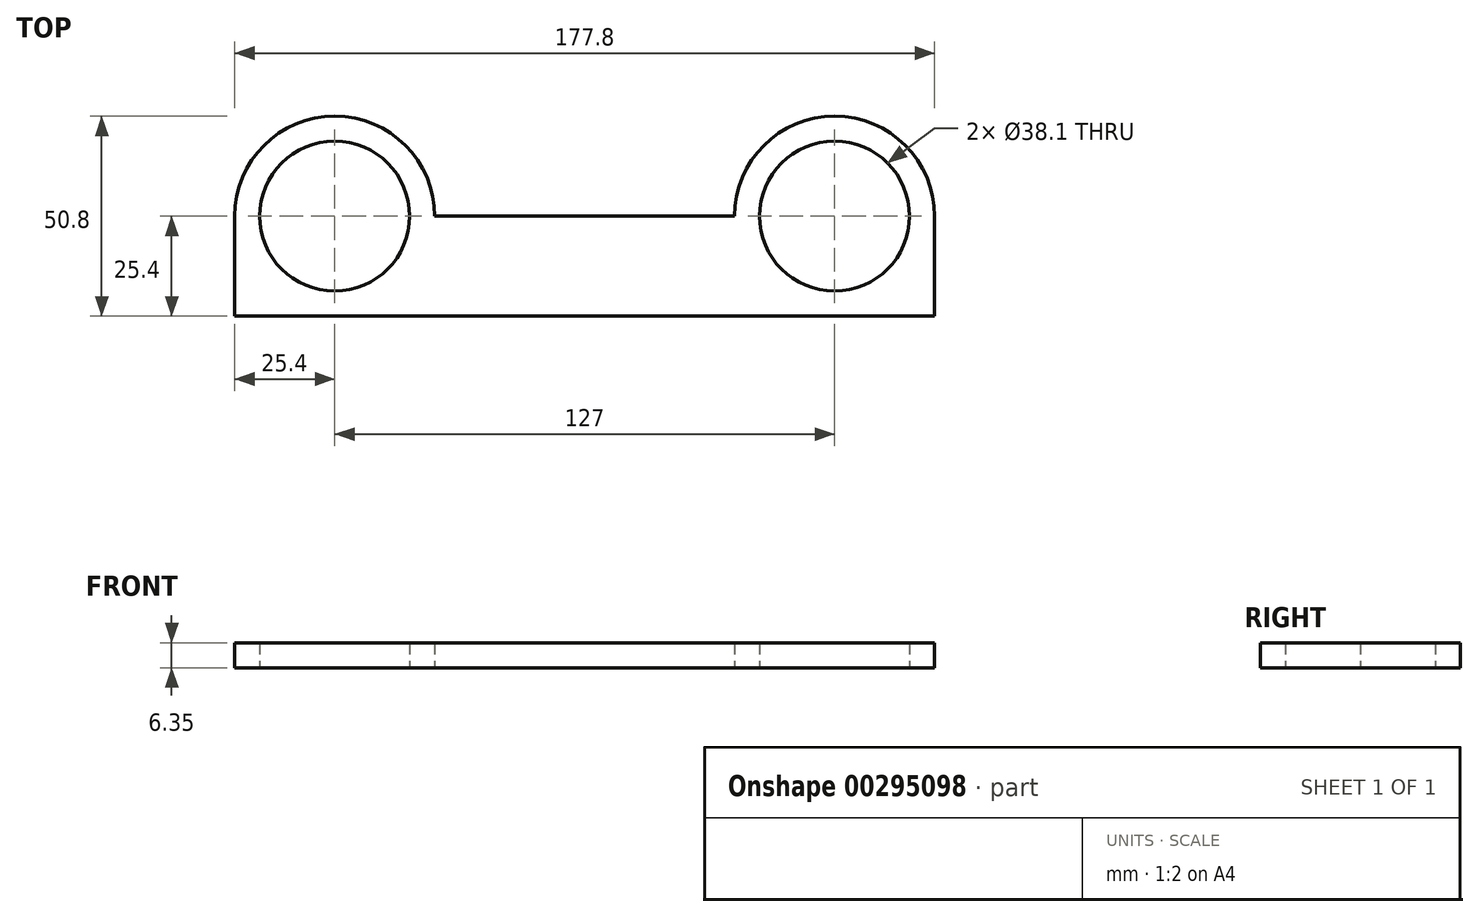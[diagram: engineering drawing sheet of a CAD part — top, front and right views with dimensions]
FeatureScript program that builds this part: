
annotation { "Feature Type Name" : "Feature", "Feature Type Description" : "" }
export const myFeature = defineFeature(function(context is Context, id is Id, definition is map)
    precondition{}
    {
        {
            var Q0;
            Q0=qCreatedBy(makeId("Top.planeOp"),FACE);
            var sketch = newSketch(context, id + "F0", { "sketchPlane" : qUnion([Q0])});
            skCircle(sketch, "E0", {"center": v(63.5, 0) * mm, "radius": 19.05 * mm});
            skCircle(sketch, "E1", {"center": v(-63.5, 0) * mm, "radius": 19.05 * mm});
            skLineSegment(sketch, "E2", {"start": v(-88.9, -25.4) * mm, "end": v(88.9, -25.4) * mm});
            skLineSegment(sketch, "E3", {"start": v(-88.9, -25.4) * mm, "end": v(-88.9, 0) * mm});
            skLineSegment(sketch, "E4", {"start": v(-63.5, 25.4) * mm, "end": v(-63.5, 25.4) * mm});
            skLineSegment(sketch, "E5", {"start": v(-38.1, 0) * mm, "end": v(-38.1, 0) * mm});
            skLineSegment(sketch, "E6", {"start": v(-38.1, 0) * mm, "end": v(38.1, 0) * mm});
            skLineSegment(sketch, "E7", {"start": v(38.1, 0) * mm, "end": v(38.1, 0) * mm});
            skLineSegment(sketch, "E8", {"start": v(63.5, 25.4) * mm, "end": v(63.5, 25.4) * mm});
            skLineSegment(sketch, "E9", {"start": v(88.9, 0) * mm, "end": v(88.9, -25.4) * mm});
            skPoint(sketch, "E10.visualSharp", {"position": v(38.1, 25.4) * mm});
            skArc(sketch, "E10.filletArc", {"start": v(63.5, 25.4) * mm, "mid": v(45.54, 17.96) * mm, "end": v(38.1, 0) * mm});
            skPoint(sketch, "E11.visualSharp", {"position": v(-38.1, 25.4) * mm});
            skArc(sketch, "E11.filletArc", {"start": v(-38.1, 0) * mm, "mid": v(-45.54, 17.96) * mm, "end": v(-63.5, 25.4) * mm});
            skPoint(sketch, "E12.visualSharp", {"position": v(88.9, 25.4) * mm});
            skArc(sketch, "E12.filletArc", {"start": v(88.9, 0) * mm, "mid": v(81.46, 17.96) * mm, "end": v(63.5, 25.4) * mm});
            skPoint(sketch, "E13.visualSharp", {"position": v(-88.9, 25.4) * mm});
            skArc(sketch, "E13.filletArc", {"start": v(-63.5, 25.4) * mm, "mid": v(-81.46, 17.96) * mm, "end": v(-88.9, 0) * mm});
            skSolve(sketch);
        }
        {
            var Q0;
            Q0=makeQuery(id+"F0.imprint","IMPRINT",FACE,{"disambiguationData":[TD([[makeQuery(id+"F0.imprint","IMPRINT",EDGE,{"derivedFrom":sQuery(id+"F0.wireOp",EDGE,"E0")}),-1.0]])]});
            extrude(context, id + "F1", {"entities" : qUnion([Q0]), "depth" : 6.35 * mm});
        }
    });
